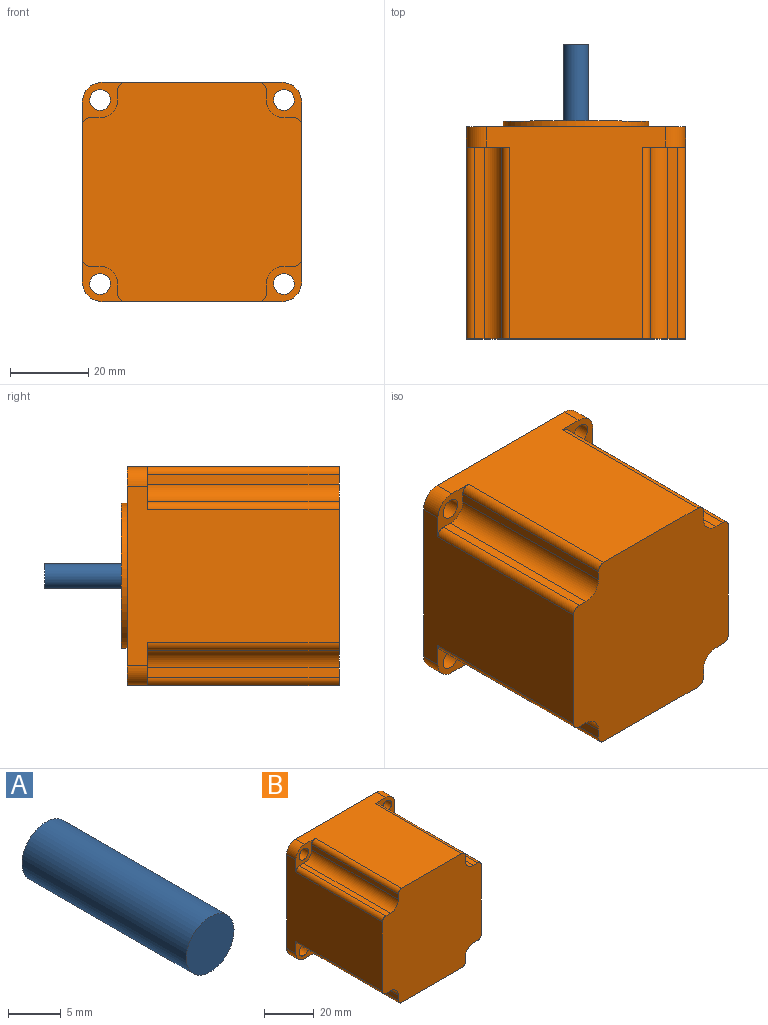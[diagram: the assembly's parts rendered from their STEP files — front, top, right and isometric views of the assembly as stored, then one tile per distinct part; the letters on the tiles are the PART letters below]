
ASSEMBLY  parts=2 mates=1
PART A: 3 faces, bbox 6.4x22x6.4 mm
  f0: cylinder r=3.2mm len=22mm, axis (0,1,0), area 442.3mm2, adj f1,f2
  f1: plane 6.4x6.4mm, normal (0,-1,0), area 32.2mm2, adj f0
  f2: plane 6.4x6.4mm, normal (0,1,0), area 32.2mm2, adj f0
PART B: 42 faces, bbox 56x55.7x56 mm
  f0: plane 11x11mm, normal (0,-1,0), area 50.9mm2, adj f3,f4,f6,f26,f27,f28,f30,f39
  f1: plane 11x11mm, normal (0,-1,0), area 50.9mm2, adj f3,f9,f10,f23,f24,f25,f33,f37
  f2: plane 11x11mm, normal (0,-1,0), area 50.9mm2, adj f4,f5,f7,f17,f18,f19,f31,f34
  f3: plane 54.2x46mm, normal (1,0,0), area 1905.2mm2, adj f0,f1,f12,f29,f30,f33,f38,f39
  f4: plane 54.2x46mm, normal (0,0,1), area 1905.2mm2, adj f0,f2,f12,f29,f30,f31,f40,f41
  f5: plane 54.2x46mm, normal (-1,0,0), area 1905.2mm2, adj f2,f11,f12,f29,f31,f32,f34,f35
  f6: cylinder r=2.65mm len=5.3mm, axis (0,1,0), area 86.6mm2, adj f0,f12
  f7: cylinder r=2.65mm len=5.3mm, axis (0,1,0), area 86.6mm2, adj f2,f12
  f8: cylinder r=2.65mm len=5.3mm, axis (0,1,0), area 86.6mm2, adj f11,f12
  f9: plane 54.2x46mm, normal (0,0,-1), area 1905.2mm2, adj f1,f11,f12,f29,f32,f33,f36,f37
  f10: cylinder r=2.65mm len=5.3mm, axis (0,1,0), area 86.6mm2, adj f1,f12
  f11: plane 11x11mm, normal (0,-1,0), area 50.9mm2, adj f5,f8,f9,f20,f21,f22,f32,f35
  f12: plane 56x56mm, normal (0,1,0), area 1945.3mm2, adj f3,f4,f5,f6,f7,f8,f9,f10
  f13: cylinder r=18.55mm len=37.1mm, axis (0,-1,0), area 174.8mm2, adj f12,f14
  f14: plane 37.1x37.1mm, normal (0,1,0), area 982.5mm2, adj f13,f15
  f15: cylinder r=5.6mm len=11.2mm, axis (0,1,0), area 88mm2, adj f14,f16
  f16: plane 11.2x11.2mm, normal (0,1,0), area 98.5mm2, adj f15
  f17: plane 49x2.5mm, normal (-1,0,0), area 122.5mm2, adj f2,f18,f29,f41
  f18: cylinder r=4.5mm len=49mm, axis (0,1,0), area 346.4mm2, adj f2,f17,f19,f29
  f19: plane 49x2.5mm, normal (0,0,1), area 122.5mm2, adj f2,f18,f29,f34
  f20: plane 49x2.5mm, normal (0,0,-1), area 122.5mm2, adj f11,f21,f29,f35
  f21: cylinder r=4.5mm len=49mm, axis (0,1,0), area 346.4mm2, adj f11,f20,f22,f29
  f22: plane 49x2.5mm, normal (-1,0,0), area 122.5mm2, adj f11,f21,f29,f36
  f23: plane 49x2.5mm, normal (1,0,0), area 122.5mm2, adj f1,f24,f29,f37
  f24: cylinder r=4.5mm len=49mm, axis (0,1,0), area 346.4mm2, adj f1,f23,f25,f29
  f25: plane 49x2.5mm, normal (0,0,-1), area 122.5mm2, adj f1,f24,f29,f38
  f26: plane 49x2.5mm, normal (0,0,1), area 122.5mm2, adj f0,f27,f29,f39
  f27: cylinder r=4.5mm len=49mm, axis (0,1,0), area 346.4mm2, adj f0,f26,f28,f29
  f28: plane 49x2.5mm, normal (1,0,0), area 122.5mm2, adj f0,f27,f29,f40
  f29: plane 56x56mm, normal (0,-1,0), area 2822.5mm2, adj f3,f4,f5,f9,f17,f18,f19,f20
  f30: cylinder r=5mm len=5.2mm, axis (0,1,0), area 40.8mm2, adj f0,f3,f4,f12
  f31: cylinder r=5mm len=5.2mm, axis (0,-1,0), area 40.8mm2, adj f2,f4,f5,f12
  f32: cylinder r=5mm len=5.2mm, axis (0,1,0), area 40.8mm2, adj f5,f9,f11,f12
  f33: cylinder r=5mm len=5.2mm, axis (0,-1,0), area 40.8mm2, adj f1,f3,f9,f12
  f34: cylinder r=2mm len=49mm, axis (0,1,0), area 153.9mm2, adj f2,f5,f19,f29
  f35: cylinder r=2mm len=49mm, axis (0,1,0), area 153.9mm2, adj f5,f11,f20,f29
  f36: cylinder r=2mm len=49mm, axis (0,1,0), area 153.9mm2, adj f9,f11,f22,f29
  f37: cylinder r=2mm len=49mm, axis (0,1,0), area 153.9mm2, adj f1,f9,f23,f29
  f38: cylinder r=2mm len=49mm, axis (0,-1,0), area 153.9mm2, adj f1,f3,f25,f29
  f39: cylinder r=2mm len=49mm, axis (0,-1,0), area 153.9mm2, adj f0,f3,f26,f29
  f40: cylinder r=2mm len=49mm, axis (0,1,0), area 153.9mm2, adj f0,f4,f28,f29
  f41: cylinder r=2mm len=49mm, axis (0,1,0), area 153.9mm2, adj f2,f4,f17,f29
PLACE A t=(0,21,0)mm
PLACE B at identity
MATE revolute A.f0 <-> B.f15  axis (0,-1,0) through (0,-1,0)mm
